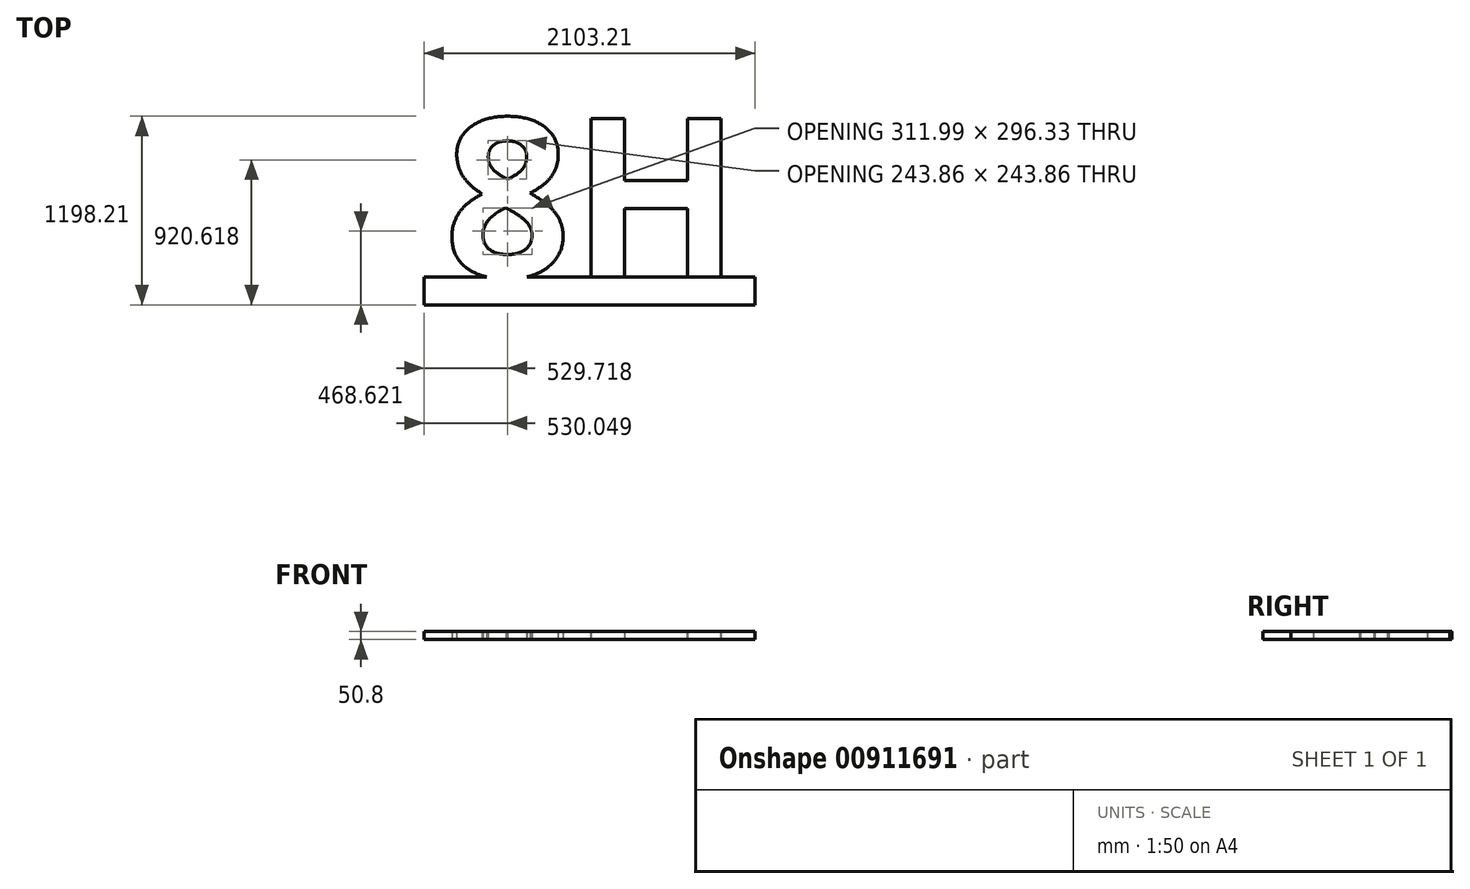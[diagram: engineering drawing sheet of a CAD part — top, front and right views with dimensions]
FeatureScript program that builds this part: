
annotation { "Feature Type Name" : "Feature", "Feature Type Description" : "" }
export const myFeature = defineFeature(function(context is Context, id is Id, definition is map)
    precondition{}
    {
        {
            var Q0;
            Q0=qCreatedBy(makeId("Top.planeOp"),FACE);
            var sketch = newSketch(context, id + "F0", { "sketchPlane" : qUnion([Q0])});
            skText(sketch, "E0", { "text": "8H", "fontName": "OpenSans-Bold.ttf"});
            skLineSegment(sketch, "E1.bottom", {"start": v(-654.5, -687.74) * mm, "end": v(1448.71, -687.74) * mm});
            skLineSegment(sketch, "E1.top", {"start": v(-654.5, -509.94) * mm, "end": v(1448.71, -509.94) * mm});
            skLineSegment(sketch, "E1.left", {"start": v(-654.5, -687.74) * mm, "end": v(-654.5, -509.94) * mm});
            skLineSegment(sketch, "E1.right", {"start": v(1448.71, -687.74) * mm, "end": v(1448.71, -509.94) * mm});
            const initialGuessF0  = {"E0": [-0.5275, -0.50994, 1, 0, 1.016]};
            skSetInitialGuess(sketch, initialGuessF0);
            skSolve(sketch);
        }
        {
            var Q0;
            Q0=makeQuery(id+"F0.imprint","IMPRINT",FACE,{"disambiguationData":[TD([[makeQuery(id+"F0.imprint","IMPRINT",EDGE,{"derivedFrom":sQuery(id+"F0.wireOp",EDGE,"E0.sketch_text.stroke-0")}),-1.0]])]});
            var Q1;
            {var subQ1=sQuery(id+"F0.wireOp",EDGE,"E0.sketch_text.stroke-32");Q1=makeQuery(id+"F0.imprint","IMPRINT",FACE,{"disambiguationData":[TD([[makeQuery(id+"F0.imprint","IMPRINT",EDGE,{"derivedFrom":subQ1}),-1.0]])]});}
            var Q2;
            Q2=makeQuery(id+"F0.imprint","IMPRINT",FACE,{"disambiguationData":[TD([[makeQuery(id+"F0.imprint","IMPRINT",EDGE,{"derivedFrom":sQuery(id+"F0.wireOp",EDGE,"E1.bottom")}),1.0]])]});
            var Q3;
            {var subQ0=sQuery(id+"F0.wireOp",EDGE,"E0.sketch_text.stroke-8");var subQ1=sQuery(id+"F0.wireOp",EDGE,"E0.sketch_text.stroke-7");var subQ2=makeQuery(id+"F0.imprint","INTERSECT",VERTEX,{"derivedFrom":[subQ1,subQ0]});Q3=makeQuery(id+"F0.imprint","IMPRINT",FACE,{"disambiguationData":[TD([[makeQuery(id+"F0.imprint","IMPRINT",EDGE,{"disambiguationData":[TD([[subQ2,1.0]])],"derivedFrom":subQ1}),-1.0]])]});}
            extrude(context, id + "F1", {"entities" : qUnion([Q0, Q1, Q2, Q3]), "depth" : 50.8 * mm, "offsetDistance" : 25.4 * mm});
        }
    });
